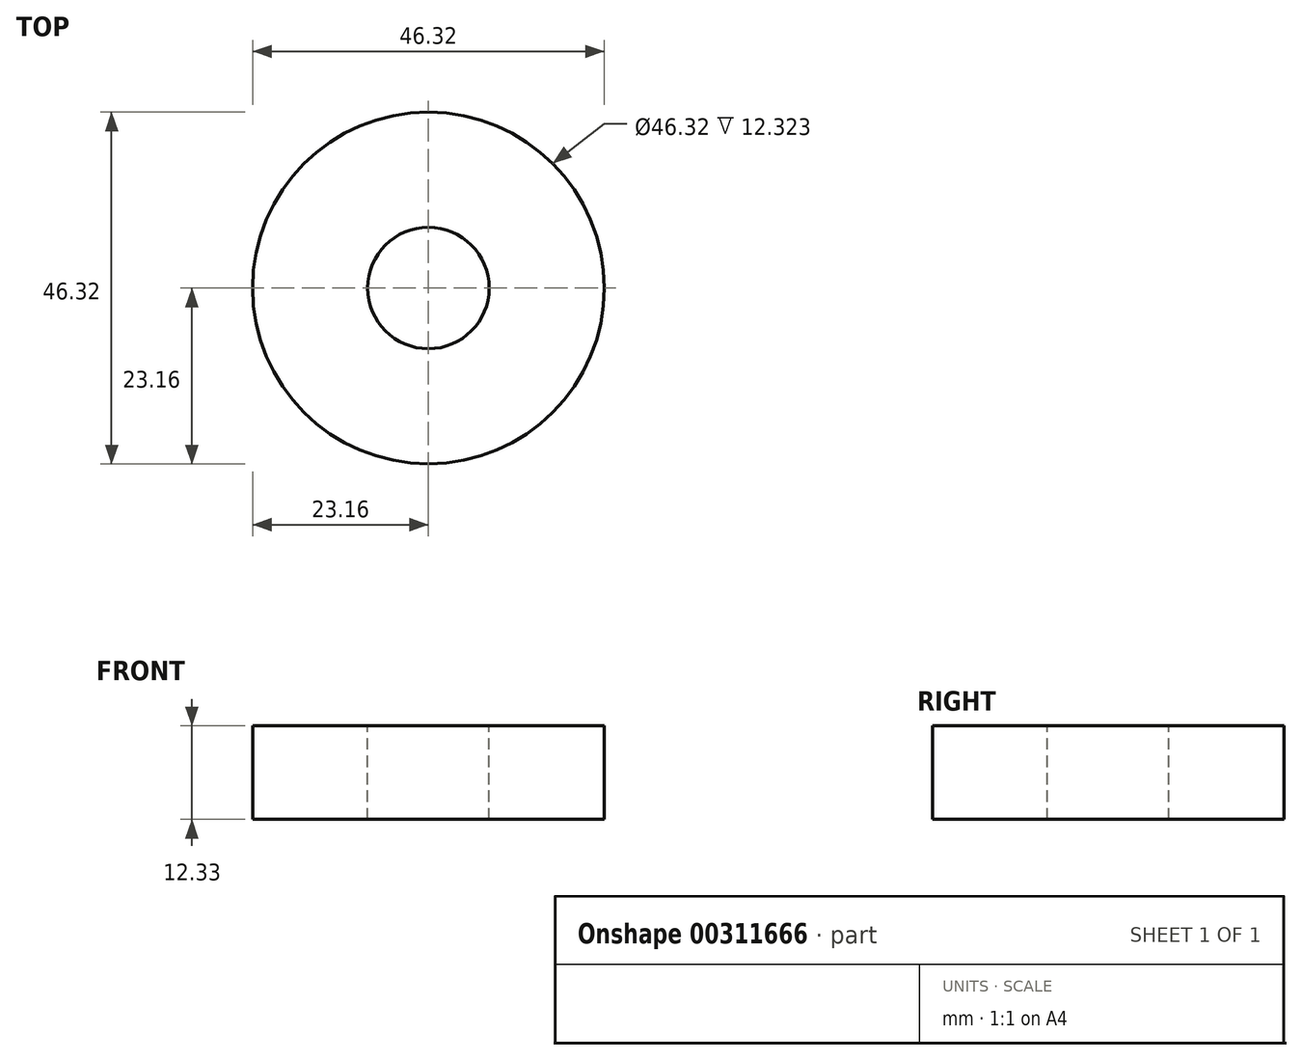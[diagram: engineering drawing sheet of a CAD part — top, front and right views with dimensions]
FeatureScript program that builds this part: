
annotation { "Feature Type Name" : "Feature", "Feature Type Description" : "" }
export const myFeature = defineFeature(function(context is Context, id is Id, definition is map)
    precondition{}
    {
        {
            var Q0;
            Q0=qCreatedBy(makeId("Front.planeOp"),FACE);
            var sketch = newSketch(context, id + "F0", { "sketchPlane" : qUnion([Q0])});
            skLineSegment(sketch, "E0", {"start": v(0, 0) * mm, "end": v(0, 28.2) * mm, "construction": true});
            skLineSegment(sketch, "E1.bottom", {"start": v(8, 17.23) * mm, "end": v(23.16, 17.23) * mm});
            skLineSegment(sketch, "E1.top", {"start": v(8, 4.9) * mm, "end": v(23.16, 4.9) * mm});
            skLineSegment(sketch, "E1.left", {"start": v(8, 17.23) * mm, "end": v(8, 4.9) * mm});
            skLineSegment(sketch, "E1.right", {"start": v(23.16, 17.23) * mm, "end": v(23.16, 4.9) * mm});
            skSolve(sketch);
        }
        {
            var Q0;
            Q0 = qConstructionFilter(qBodyType(qCreatedBy(id + "F0" ,EDGE), BodyType.WIRE), ConstructionObject.NO);
            var Q1;
            Q1=sQuery(id+"F0.wireOp",EDGE,"E0");
            revolve(context, id + "F1", {"bodyType" : ToolBodyType.SURFACE, "surfaceEntities" : qUnion([Q0]), "axis" : qUnion([Q1]), "revolveType" : RevolveType.FULL});
        }
    });
